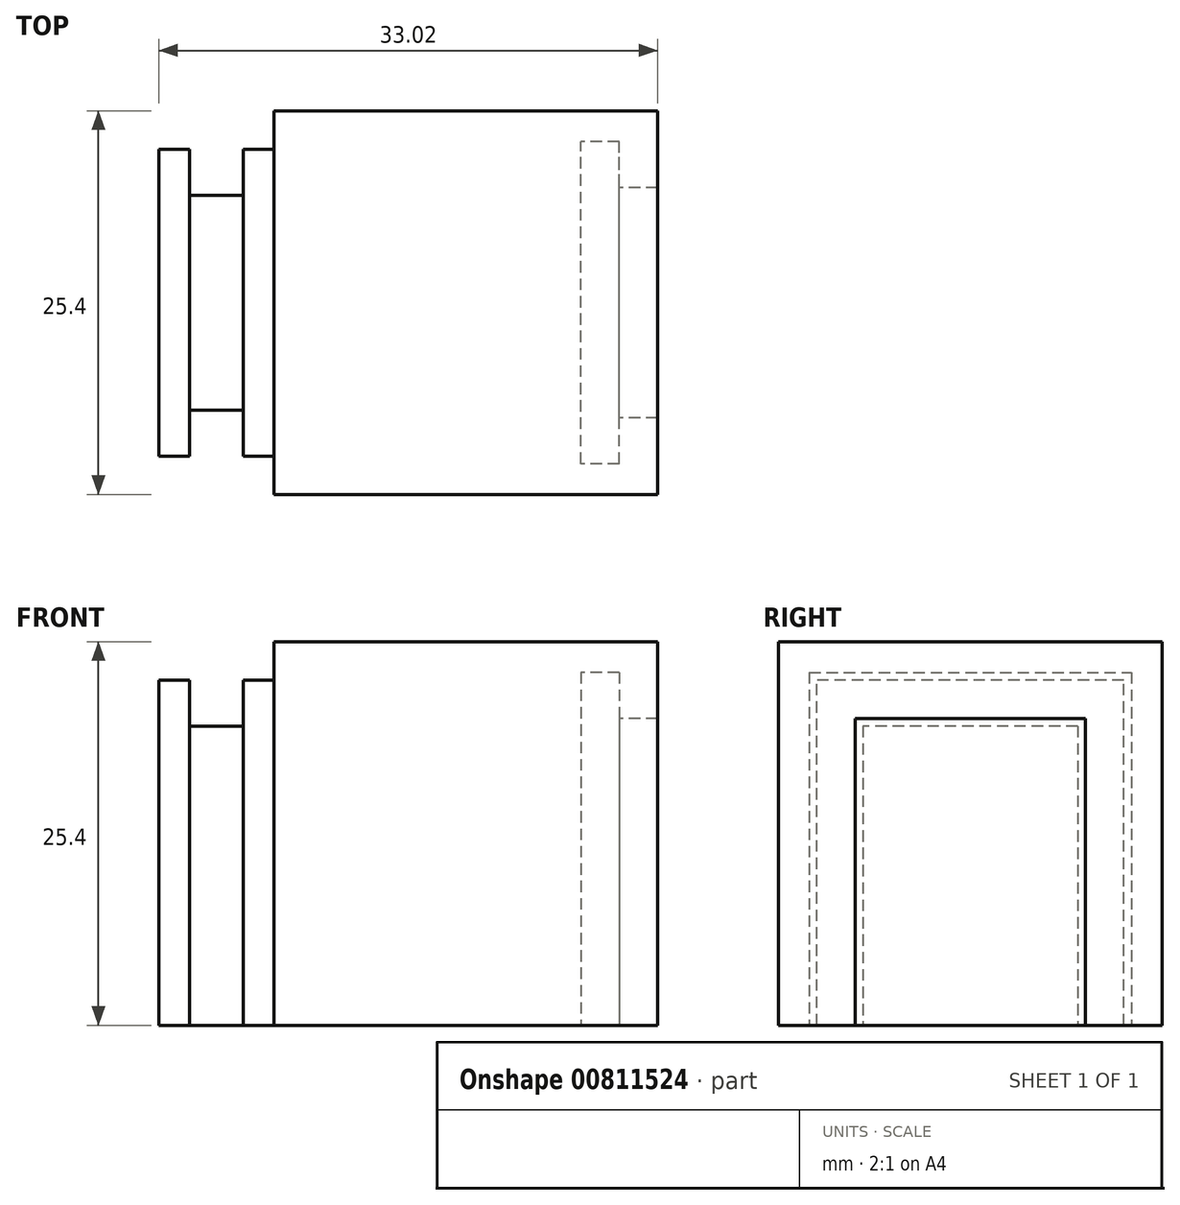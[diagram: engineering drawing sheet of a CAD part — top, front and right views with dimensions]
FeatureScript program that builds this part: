
annotation { "Feature Type Name" : "Feature", "Feature Type Description" : "" }
export const myFeature = defineFeature(function(context is Context, id is Id, definition is map)
    precondition{}
    {
        {
            var Q0;
            Q0=qCreatedBy(makeId("Top.planeOp"),FACE);
            var sketch = newSketch(context, id + "F0", { "sketchPlane" : qUnion([Q0])});
            skLineSegment(sketch, "E0.bottom", {"start": v(12.7, -12.7) * mm, "end": v(-12.7, -12.7) * mm});
            skLineSegment(sketch, "E0.top", {"start": v(12.7, 12.7) * mm, "end": v(-12.7, 12.7) * mm});
            skLineSegment(sketch, "E0.left", {"start": v(12.7, -12.7) * mm, "end": v(12.7, 12.7) * mm});
            skLineSegment(sketch, "E0.right", {"start": v(-12.7, -12.7) * mm, "end": v(-12.7, 12.7) * mm});
            skPoint(sketch, "E0.middle", {"position": v(0, 0) * mm});
            skSolve(sketch);
        }
        {
            var Q0;
            Q0=makeQuery(id+"F0.imprint","IMPRINT",FACE,{"disambiguationData":[TD([[makeQuery(id+"F0.imprint","IMPRINT",EDGE,{"derivedFrom":sQuery(id+"F0.wireOp",EDGE,"E0.bottom")}),-1.0]])]});
            extrude(context, id + "F1", {"entities" : qUnion([Q0]), "depth" : 25.4 * mm, "offsetDistance" : 25.4 * mm});
        }
        {
            var Q0;
            Q0=makeQuery(id+"F1.opExtrude","SWEPT_FACE",FACE,{"disambiguationData":[OSD([sQuery(id+"F0.wireOp",EDGE,"E0.right")])]});
            var sketch = newSketch(context, id + "F2", { "sketchPlane" : qUnion([Q0])});
            skLineSegment(sketch, "E1", {"start": v(-12.7, 0) * mm, "end": v(-10.16, 0) * mm});
            skLineSegment(sketch, "E2", {"start": v(-10.16, 0) * mm, "end": v(-10.16, 22.86) * mm});
            skLineSegment(sketch, "E3", {"start": v(-10.16, 22.86) * mm, "end": v(10.16, 22.86) * mm});
            skLineSegment(sketch, "E4", {"start": v(10.16, 22.86) * mm, "end": v(10.16, 0) * mm});
            skLineSegment(sketch, "E5", {"start": v(10.16, 0) * mm, "end": v(12.7, 0) * mm});
            skSolve(sketch);
        }
        {
            var Q0;
            {var subQ0=sQuery(id+"F2.wireOp",EDGE,"E2");Q0=makeQuery(id+"F2.imprint","IMPRINT",FACE,{"disambiguationData":[TD([[makeQuery(id+"F2.imprint","IMPRINT",EDGE,{"derivedFrom":subQ0}),-1.0]])]});}
            extrude(context, id + "F3", {"entities" : qUnion([Q0]), "operationType" : NewBodyOperationType.ADD, "depth" : 7.62 * mm, "offsetDistance" : 25.4 * mm});
        }
        {
            var Q0;
            Q0=makeQuery(id+"F3.opExtrude","SWEPT_FACE",FACE,{"disambiguationData":[OSD([sQuery(id+"F2.wireOp",EDGE,"E3")])]});
            var sketch = newSketch(context, id + "F4", { "sketchPlane" : qUnion([Q0])});
            skLineSegment(sketch, "E6", {"start": v(-20.32, 10.16) * mm, "end": v(-18.29, 10.16) * mm});
            skLineSegment(sketch, "E7.bottom", {"start": v(-18.29, 10.16) * mm, "end": v(-14.73, 10.16) * mm});
            skLineSegment(sketch, "E7.top", {"start": v(-18.29, -10.16) * mm, "end": v(-14.73, -10.16) * mm});
            skLineSegment(sketch, "E7.left", {"start": v(-18.29, 10.16) * mm, "end": v(-18.29, -10.16) * mm});
            skLineSegment(sketch, "E7.right", {"start": v(-14.73, 10.16) * mm, "end": v(-14.73, -10.16) * mm});
            skSolve(sketch);
        }
        {
            var Q0;
            Q0=makeQuery(id+"F4.imprint","IMPRINT",FACE,{"disambiguationData":[TD([[makeQuery(id+"F4.imprint","IMPRINT",EDGE,{"derivedFrom":sQuery(id+"F4.wireOp",EDGE,"E7.bottom")}),-1.0]])]});
            extrude(context, id + "F5", {"entities" : qUnion([Q0]), "operationType" : NewBodyOperationType.REMOVE, "oppositeDirection" : true, "depth" : 3.05 * mm, "offsetDistance" : 25.4 * mm});
        }
        {
            var Q0;
            Q0=makeQuery(id+"F3.opExtrude","SWEPT_FACE",FACE,{"disambiguationData":[OSD([sQuery(id+"F2.wireOp",EDGE,"E4")])]});
            var sketch = newSketch(context, id + "F6", { "sketchPlane" : qUnion([Q0])});
            skLineSegment(sketch, "E8.bottom", {"start": v(-18.29, 19.81) * mm, "end": v(-14.73, 19.81) * mm});
            skLineSegment(sketch, "E8.top", {"start": v(-18.29, 0) * mm, "end": v(-14.73, 0) * mm});
            skLineSegment(sketch, "E8.left", {"start": v(-18.29, 19.81) * mm, "end": v(-18.29, 0) * mm});
            skLineSegment(sketch, "E8.right", {"start": v(-14.73, 19.81) * mm, "end": v(-14.73, 0) * mm});
            skSolve(sketch);
        }
        {
            var Q0;
            Q0=makeQuery(id+"F6.imprint","IMPRINT",FACE,{"disambiguationData":[TD([[makeQuery(id+"F6.imprint","IMPRINT",EDGE,{"derivedFrom":sQuery(id+"F6.wireOp",EDGE,"E8.bottom")}),-1.0]])]});
            extrude(context, id + "F7", {"entities" : qUnion([Q0]), "operationType" : NewBodyOperationType.REMOVE, "oppositeDirection" : true, "depth" : 3.05 * mm, "offsetDistance" : 25.4 * mm});
        }
        {
            var Q0;
            Q0=makeQuery(id+"F3.opExtrude","SWEPT_FACE",FACE,{"disambiguationData":[OSD([sQuery(id+"F2.wireOp",EDGE,"E2")])]});
            var sketch = newSketch(context, id + "F8", { "sketchPlane" : qUnion([Q0])});
            skLineSegment(sketch, "E9.bottom", {"start": v(14.73, 19.81) * mm, "end": v(18.29, 19.81) * mm});
            skLineSegment(sketch, "E9.top", {"start": v(14.73, 0) * mm, "end": v(18.29, 0) * mm});
            skLineSegment(sketch, "E9.left", {"start": v(14.73, 19.81) * mm, "end": v(14.73, 0) * mm});
            skLineSegment(sketch, "E9.right", {"start": v(18.29, 19.81) * mm, "end": v(18.29, 0) * mm});
            skSolve(sketch);
        }
        {
            var Q0;
            Q0=makeQuery(id+"F8.imprint","IMPRINT",FACE,{"disambiguationData":[TD([[makeQuery(id+"F8.imprint","IMPRINT",EDGE,{"derivedFrom":sQuery(id+"F8.wireOp",EDGE,"E9.bottom")}),1.0]])]});
            extrude(context, id + "F9", {"entities" : qUnion([Q0]), "operationType" : NewBodyOperationType.REMOVE, "oppositeDirection" : true, "depth" : 3.05 * mm, "offsetDistance" : 25.4 * mm});
        }
        {
            var Q0;
            Q0=makeQuery(id+"F1.opExtrude","SWEPT_BODY",BODY,{"disambiguationData":[OSD([sQuery(id+"F0.wireOp",EDGE,"E0.bottom"),sQuery(id+"F0.wireOp",EDGE,"E0.top"),sQuery(id+"F0.wireOp",EDGE,"E0.left"),sQuery(id+"F0.wireOp",EDGE,"E0.right")])]});
            transform(context, id + "F10", {"entities" : qUnion([Q0]), "transformType" : TransformType.TRANSLATION_3D, "dx" : -54.1 * mm, "dy" : 0 * mm, "dz" : 0 * mm, "makeCopy" : true});
        }
        {
            var Q0;
            Q0=makeQuery(id+"F10.opPattern","COPY",BODY,{"derivedFrom":makeQuery(id+"F1.opExtrude","SWEPT_BODY",BODY,{"disambiguationData":[OSD([sQuery(id+"F0.wireOp",EDGE,"E0.bottom"),sQuery(id+"F0.wireOp",EDGE,"E0.top"),sQuery(id+"F0.wireOp",EDGE,"E0.left"),sQuery(id+"F0.wireOp",EDGE,"E0.right")])]}),"instanceName":"1"});
            deleteBodies(context, id + "F11", {"entities" : qUnion([Q0])});
        }
        {
            var Q0;
            {var subQ0=sQuery(id+"F0.wireOp",EDGE,"E0.right");Q0=makeQuery(id+"F3.boolean.opBoolean","MERGE",FACE,{"derivedFrom":[makeQuery(id+"F1.opExtrude","CAP_FACE",FACE,{"disambiguationData":[OSD([sQuery(id+"F0.wireOp",EDGE,"E0.bottom"),sQuery(id+"F0.wireOp",EDGE,"E0.top"),sQuery(id+"F0.wireOp",EDGE,"E0.left"),subQ0])],"isStart":true}),makeQuery(id+"F3.opExtrude","SWEPT_FACE",FACE,{"disambiguationData":[OSD([subQ0])]})]});}
            var sketch = newSketch(context, id + "F12", { "sketchPlane" : qUnion([Q0])});
            skLineSegment(sketch, "E10", {"start": v(12.7, 12.7) * mm, "end": v(12.7, 7.62) * mm});
            skLineSegment(sketch, "E11.bottom", {"start": v(12.7, 7.62) * mm, "end": v(10.16, 7.62) * mm});
            skLineSegment(sketch, "E11.top", {"start": v(12.7, -7.62) * mm, "end": v(10.16, -7.62) * mm});
            skLineSegment(sketch, "E11.left", {"start": v(12.7, 7.62) * mm, "end": v(12.7, -7.62) * mm});
            skLineSegment(sketch, "E11.right", {"start": v(10.16, 7.62) * mm, "end": v(10.16, -7.62) * mm});
            skLineSegment(sketch, "E12.bottom", {"start": v(10.16, 10.67) * mm, "end": v(7.62, 10.67) * mm});
            skLineSegment(sketch, "E12.top", {"start": v(10.16, -10.67) * mm, "end": v(7.62, -10.67) * mm});
            skLineSegment(sketch, "E12.left", {"start": v(10.16, 10.67) * mm, "end": v(10.16, -10.67) * mm});
            skLineSegment(sketch, "E12.right", {"start": v(7.62, 10.67) * mm, "end": v(7.62, -10.67) * mm});
            skPoint(sketch, "E12.middle", {"position": v(8.9, 0) * mm});
            skSolve(sketch);
        }
        {
            var Q0;
            {var subQ3=sQuery(id+"F12.wireOp",EDGE,"E12.bottom");Q0=makeQuery(id+"F12.imprint","IMPRINT",FACE,{"disambiguationData":[TD([[makeQuery(id+"F12.imprint","IMPRINT",EDGE,{"derivedFrom":subQ3}),1.0]])]});}
            extrude(context, id + "F13", {"entities" : qUnion([Q0]), "operationType" : NewBodyOperationType.REMOVE, "oppositeDirection" : true, "depth" : 23.37 * mm, "offsetDistance" : 25.4 * mm});
        }
        {
            var Q0;
            {var subQ0=sQuery(id+"F12.wireOp",EDGE,"E11.bottom");Q0=makeQuery(id+"F12.imprint","IMPRINT",FACE,{"disambiguationData":[TD([[makeQuery(id+"F12.imprint","IMPRINT",EDGE,{"derivedFrom":subQ0}),1.0]])]});}
            extrude(context, id + "F14", {"entities" : qUnion([Q0]), "operationType" : NewBodyOperationType.REMOVE, "oppositeDirection" : true, "depth" : 20.32 * mm, "offsetDistance" : 25.4 * mm});
        }
    });
